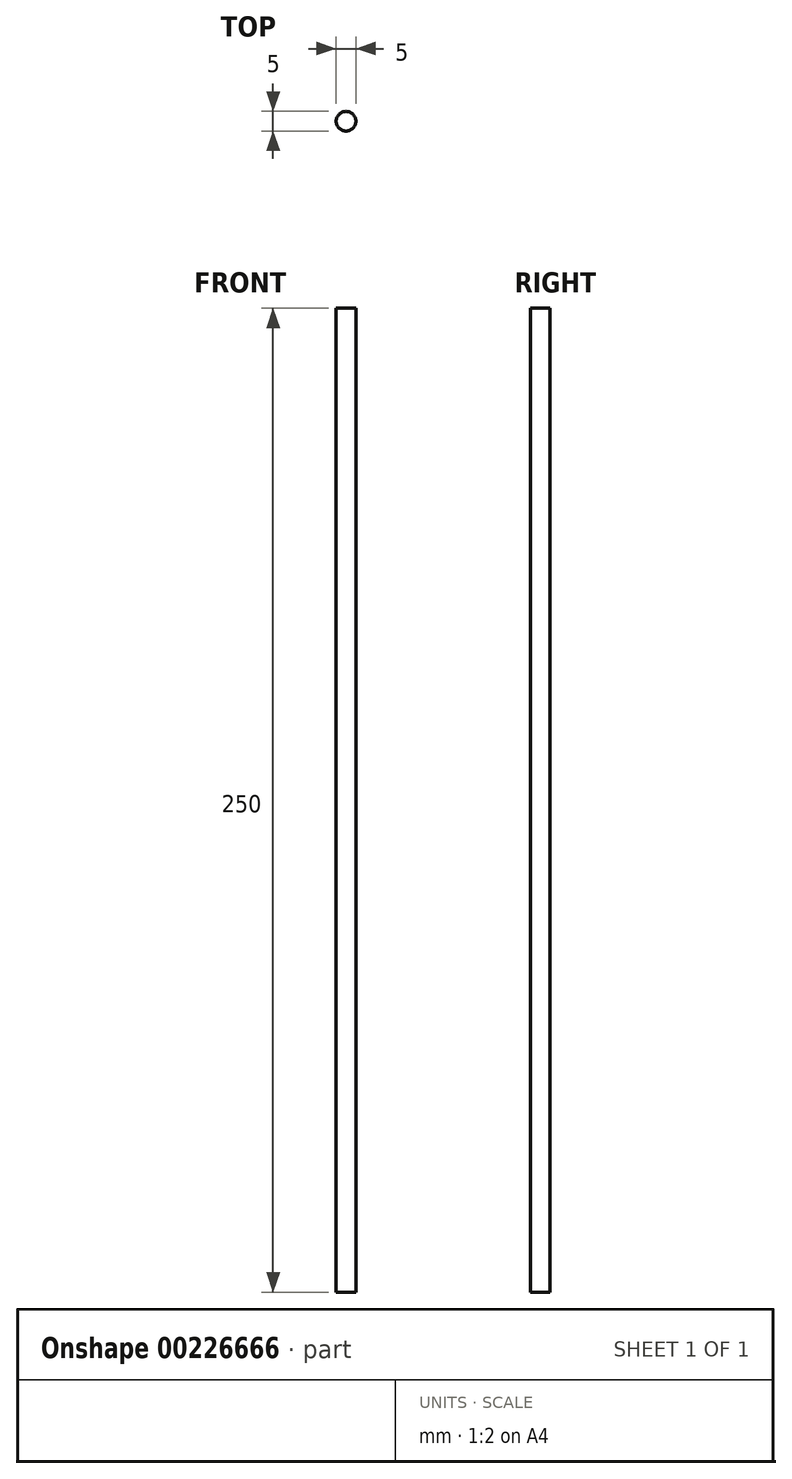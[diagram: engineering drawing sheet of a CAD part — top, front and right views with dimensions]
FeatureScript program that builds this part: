
annotation { "Feature Type Name" : "Feature", "Feature Type Description" : "" }
export const myFeature = defineFeature(function(context is Context, id is Id, definition is map)
    precondition{}
    {
        {
            var Q0;
            Q0=qCreatedBy(makeId("Top.planeOp"),FACE);
            var sketch = newSketch(context, id + "F0", { "sketchPlane" : qUnion([Q0])});
            skCircle(sketch, "E0", {"center": v(0, 0) * mm, "radius": 2.5 * mm});
            skSolve(sketch);
        }
        {
            var Q0;
            Q0 = qSketchRegion(id + "F0", true);
            extrude(context, id + "F1", {"entities" : qUnion([Q0]), "depth" : 250 * mm});
        }
    });
